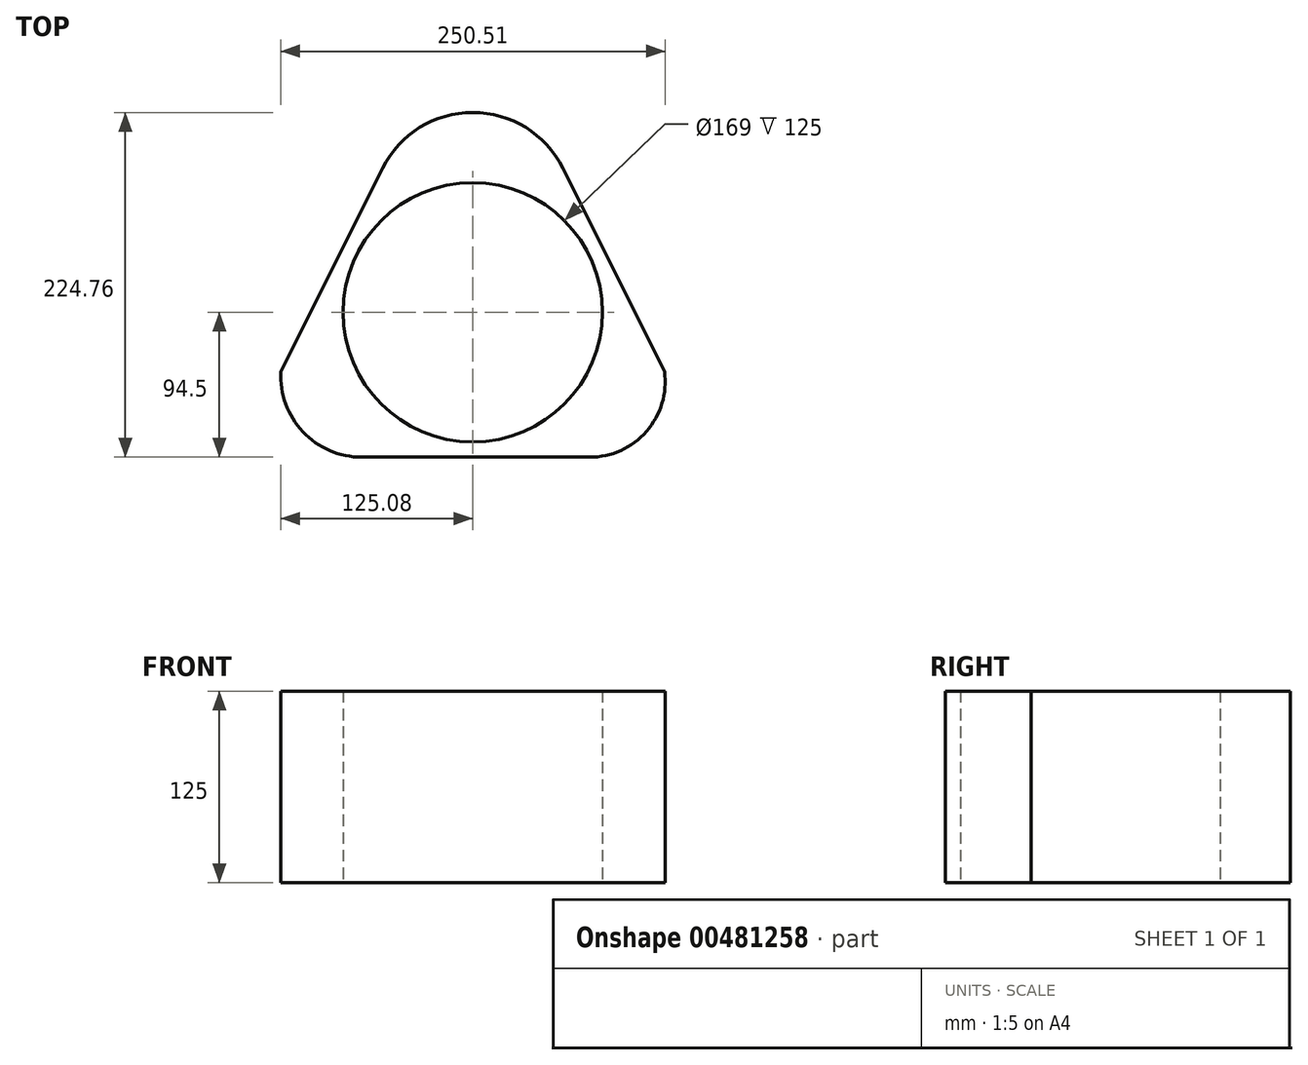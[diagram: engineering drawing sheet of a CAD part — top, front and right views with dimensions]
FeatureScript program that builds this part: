
annotation { "Feature Type Name" : "Feature", "Feature Type Description" : "" }
export const myFeature = defineFeature(function(context is Context, id is Id, definition is map)
    precondition{}
    {
        {
            var Q0;
            Q0=qCreatedBy(makeId("Top.planeOp"),FACE);
            var sketch = newSketch(context, id + "F0", { "sketchPlane" : qUnion([Q0])});
            skLineSegment(sketch, "E0", {"start": v(125, -38.69) * mm, "end": v(58.65, 94.01) * mm});
            skLineSegment(sketch, "E1", {"start": v(-58.65, 94.01) * mm, "end": v(-125, -38.69) * mm});
            skLineSegment(sketch, "E2", {"start": v(-72.24, -94.5) * mm, "end": v(76.13, -94.5) * mm});
            skCircle(sketch, "E3", {"center": v(0, 0) * mm, "radius": 84.5 * mm, "construction": true});
            skArc(sketch, "E4", {"start": v(58.65, 94.01) * mm, "mid": v(0, 130.26) * mm, "end": v(-58.65, 94.01) * mm});
            skArc(sketch, "E5", {"start": v(-125, -38.69) * mm, "mid": v(-110.64, -77.96) * mm, "end": v(-72.24, -94.5) * mm});
            skArc(sketch, "E6", {"start": v(76.13, -94.5) * mm, "mid": v(113.22, -77.68) * mm, "end": v(125, -38.69) * mm});
            skSolve(sketch);
        }
        {
            var Q0;
            Q0=makeQuery(id+"F0.imprint","IMPRINT",FACE,{"disambiguationData":[TD([[makeQuery(id+"F0.imprint","IMPRINT",EDGE,{"derivedFrom":sQuery(id+"F0.wireOp",EDGE,"E0")}),1.0]])]});
            extrude(context, id + "F1", {"entities" : qUnion([Q0]), "depth" : 125 * mm});
        }
        {
            var Q0;
            Q0=qCreatedBy(makeId("Top.planeOp"),FACE);
            var sketch = newSketch(context, id + "F2", { "sketchPlane" : qUnion([Q0])});
            skCircle(sketch, "E7", {"center": v(0, 0) * mm, "radius": 84.5 * mm});
            skSolve(sketch);
        }
        {
            var Q0;
            Q0=makeQuery(id+"F2.imprint","IMPRINT",FACE,{"disambiguationData":[TD([[makeQuery(id+"F2.imprint","IMPRINT",EDGE,{"derivedFrom":sQuery(id+"F2.wireOp",EDGE,"E7")}),1.0]])]});
            extrude(context, id + "F3", {"entities" : qUnion([Q0]), "operationType" : NewBodyOperationType.REMOVE, "depth" : 125 * mm});
        }
    });
